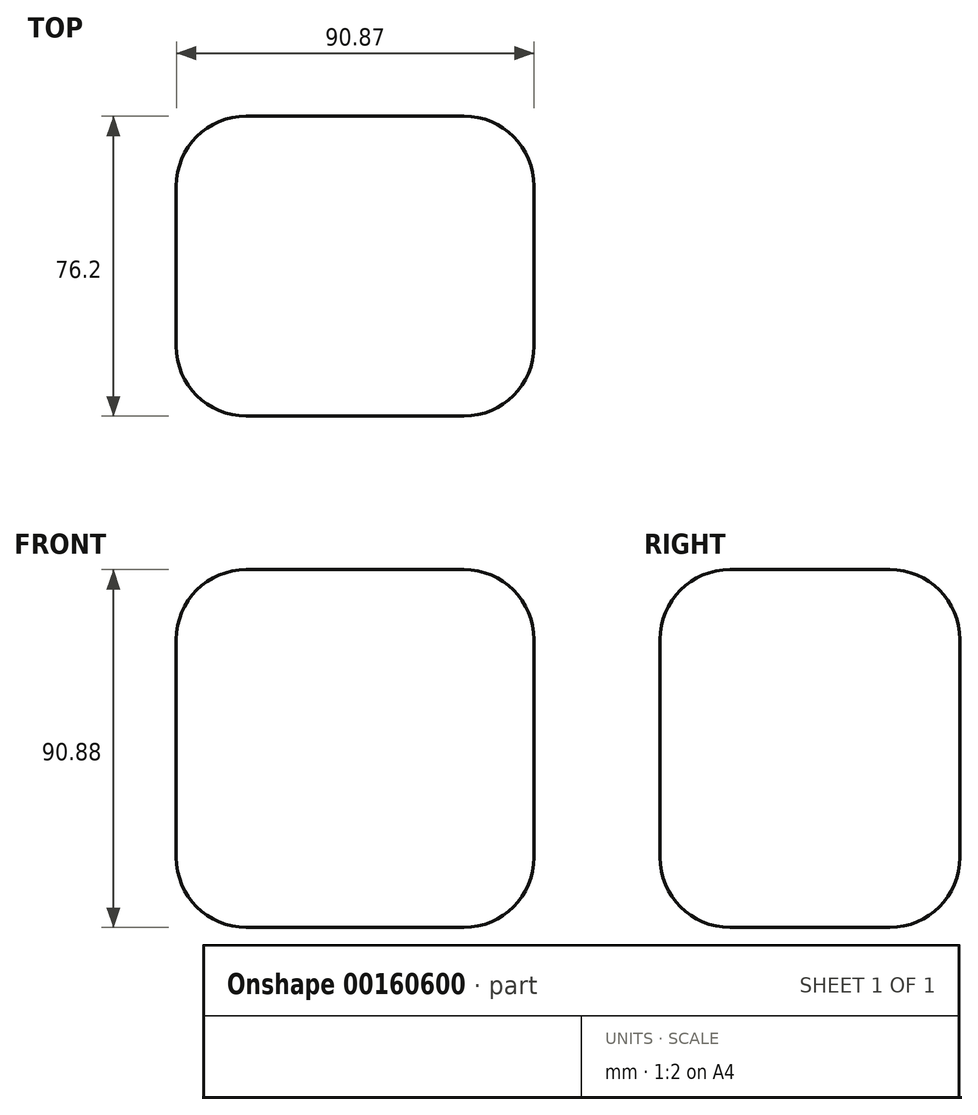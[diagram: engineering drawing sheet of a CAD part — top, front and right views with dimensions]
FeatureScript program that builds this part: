
annotation { "Feature Type Name" : "Feature", "Feature Type Description" : "" }
export const myFeature = defineFeature(function(context is Context, id is Id, definition is map)
    precondition{}
    {
        {
            var Q0;
            Q0=qCreatedBy(makeId("Front.planeOp"),FACE);
            var sketch = newSketch(context, id + "F0", { "sketchPlane" : qUnion([Q0])});
            skLineSegment(sketch, "E0.bottom", {"start": v(-44.03, 18.87) * mm, "end": v(46.84, 18.87) * mm});
            skLineSegment(sketch, "E0.top", {"start": v(-44.03, -72) * mm, "end": v(46.84, -72) * mm});
            skLineSegment(sketch, "E0.left", {"start": v(-44.03, 18.87) * mm, "end": v(-44.03, -72) * mm});
            skLineSegment(sketch, "E0.right", {"start": v(46.84, 18.87) * mm, "end": v(46.84, -72) * mm});
            skSolve(sketch);
        }
        {
            var Q0;
            Q0 = qSketchRegion(id + "F0", true);
            var Q1;
            Q1=makeQuery(id+"F0.imprint","IMPRINT",FACE,{"disambiguationData":[TD([[makeQuery(id+"F0.imprint","IMPRINT",EDGE,{"derivedFrom":sQuery(id+"F0.wireOp",EDGE,"E0.bottom")}),-1.0]])]});
            extrude(context, id + "F1", {"entities" : qUnion([Q0, Q1]), "depth" : 76.2 * mm});
        }
        {
            var Q0;
            Q0=makeQuery(id+"F1.opExtrude","SWEPT_EDGE",EDGE,{"disambiguationData":[OSD([sQuery(id+"F0.wireOp",EDGE,"E0.bottom"),sQuery(id+"F0.wireOp",EDGE,"E0.left")])]});
            var Q1;
            Q1=makeQuery(id+"F1.opExtrude","SWEPT_FACE",FACE,{"disambiguationData":[OSD([sQuery(id+"F0.wireOp",EDGE,"E0.bottom")])]});
            var Q2;
            Q2=makeQuery(id+"F1.opExtrude","SWEPT_EDGE",EDGE,{"disambiguationData":[OSD([sQuery(id+"F0.wireOp",EDGE,"E0.bottom"),sQuery(id+"F0.wireOp",EDGE,"E0.right")])]});
            var Q3;
            Q3=makeQuery(id+"F1.opExtrude","CAP_FACE",FACE,{"disambiguationData":[OSD([sQuery(id+"F0.wireOp",EDGE,"E0.bottom"),sQuery(id+"F0.wireOp",EDGE,"E0.top"),sQuery(id+"F0.wireOp",EDGE,"E0.left"),sQuery(id+"F0.wireOp",EDGE,"E0.right")])],"isStart":true});
            var Q4;
            Q4=makeQuery(id+"F1.opExtrude","CAP_FACE",FACE,{"disambiguationData":[OSD([sQuery(id+"F0.wireOp",EDGE,"E0.bottom"),sQuery(id+"F0.wireOp",EDGE,"E0.top"),sQuery(id+"F0.wireOp",EDGE,"E0.left"),sQuery(id+"F0.wireOp",EDGE,"E0.right")])],"isStart":false});
            var Q5;
            Q5=makeQuery(id+"F1.opExtrude","SWEPT_EDGE",EDGE,{"disambiguationData":[OSD([sQuery(id+"F0.wireOp",EDGE,"E0.top"),sQuery(id+"F0.wireOp",EDGE,"E0.right")])]});
            var Q6;
            Q6=makeQuery(id+"F1.opExtrude","CAP_EDGE",EDGE,{"disambiguationData":[OSD([sQuery(id+"F0.wireOp",EDGE,"E0.bottom")])],"isStart":true});
            var Q7;
            Q7=makeQuery(id+"F1.opExtrude","SWEPT_FACE",FACE,{"disambiguationData":[OSD([sQuery(id+"F0.wireOp",EDGE,"E0.left")])]});
            var Q8;
            Q8=makeQuery(id+"F1.opExtrude","CAP_EDGE",EDGE,{"disambiguationData":[OSD([sQuery(id+"F0.wireOp",EDGE,"E0.bottom")])],"isStart":false});
            var Q9;
            Q9=makeQuery(id+"F1.opExtrude","SWEPT_FACE",FACE,{"disambiguationData":[OSD([sQuery(id+"F0.wireOp",EDGE,"E0.right")])]});
            var Q10;
            Q10=makeQuery(id+"F1.opExtrude","CAP_EDGE",EDGE,{"disambiguationData":[OSD([sQuery(id+"F0.wireOp",EDGE,"E0.top")])],"isStart":false});
            var Q11;
            Q11=makeQuery(id+"F1.opExtrude","SWEPT_EDGE",EDGE,{"disambiguationData":[OSD([sQuery(id+"F0.wireOp",EDGE,"E0.top"),sQuery(id+"F0.wireOp",EDGE,"E0.left")])]});
            var Q12;
            Q12=makeQuery(id+"F1.opExtrude","SWEPT_FACE",FACE,{"disambiguationData":[OSD([sQuery(id+"F0.wireOp",EDGE,"E0.top")])]});
            var Q13;
            Q13=makeQuery(id+"F1.opExtrude","CAP_EDGE",EDGE,{"disambiguationData":[OSD([sQuery(id+"F0.wireOp",EDGE,"E0.top")])],"isStart":true});
            var Q14;
            Q14=makeQuery(id+"F1.opExtrude","CAP_EDGE",EDGE,{"disambiguationData":[OSD([sQuery(id+"F0.wireOp",EDGE,"E0.left")])],"isStart":true});
            var Q15;
            Q15=makeQuery(id+"F1.opExtrude","CAP_EDGE",EDGE,{"disambiguationData":[OSD([sQuery(id+"F0.wireOp",EDGE,"E0.left")])],"isStart":false});
            var Q16;
            Q16=makeQuery(id+"F1.opExtrude","CAP_EDGE",EDGE,{"disambiguationData":[OSD([sQuery(id+"F0.wireOp",EDGE,"E0.right")])],"isStart":false});
            var Q17;
            Q17=makeQuery(id+"F1.opExtrude","CAP_EDGE",EDGE,{"disambiguationData":[OSD([sQuery(id+"F0.wireOp",EDGE,"E0.right")])],"isStart":true});
            fillet(context, id + "F2", {"entities" : qUnion([Q0, Q1, Q2, Q3, Q4, Q5, Q6, Q7, Q8, Q9, Q10, Q11, Q12, Q13, Q14, Q15, Q16, Q17]), "radius" : 17.78 * mm, "tangentPropagation" : true, "allowEdgeOverflow" : false});
        }
    });
